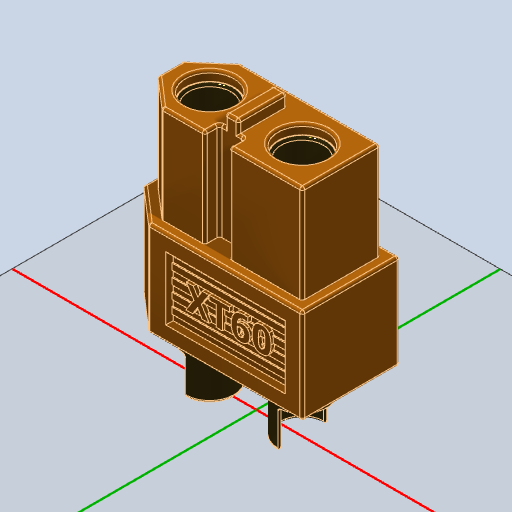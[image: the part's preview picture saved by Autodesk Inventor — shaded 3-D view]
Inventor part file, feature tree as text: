
AUTODESK INVENTOR PART (.ipt)
format: ipt  version: 2022 (Build 260153000, 153)  size: 779,776 bytes
history: native  units: mm
features: sketch x12, extrude x10, other x6, plane x4, projected_geometry x4, fillet x3, hole x1, mirror x1
ambient origin geometry x8: Origin, YZ Plane, XZ Plane, XY Plane, X Axis, Y Axis, Z Axis, Center Point
bodies: Volumenkörper1 (feature_tree)
feature tree (41):
  extrude  "Extrusion1"  Depth=8.0mm
  extrude  "Extrusion2"  Depth=3.0mm
  extrude  "Extrusion3"  Depth=3.0mm
  extrude  "Extrusion4"  Depth=0.8mm
  extrude  "Extrusion5"  Depth=1.2mm
  plane  "Arbeitsebene1"
  extrude  "Extrusion6"  TaperAngle=0.0deg  [1 undecoded]
  plane  "Arbeitsebene2"
  extrude  "Extrusion7"  Depth=4.0mm
  extrude  "Extrusion8"  Depth=8.0mm TaperAngle=0.0deg
  hole  "Bohrung1"  [1 undecoded]
  sketch  "Skizze10"  dims[d21=1.0mm d22=0.0mm d23=6.0mm]
  extrude  "Extrusion9"  Depth=6.0mm
  extrude  "Extrusion10"  Depth=4.0mm TaperAngle=0.0deg
  plane  "Arbeitsebene3"
  other  "Prägen1"
  mirror  "Spiegeln1"
  plane  "Arbeitsebene5"
  other  "Prägen2"
  fillet  "Rundung1"  [1 undecoded]
  fillet  "Rundung2"  Radius=3.5mm
  fillet  "Rundung3"  Radius=3.5mm
  sketch  "Skizze1"  dims[d0=15.6mm d1=8.0mm]
  sketch  "Skizze2"  dims[d2=2.6mm d3=3.0mm]
  sketch  "Skizze3"  dims[d4=2.6mm d5=3.0mm]
  sketch  "Skizze4"  dims[d6=7.8mm d7=0.0mm d8=0.8mm]
  sketch  "Skizze5"  dims[d9=2.0mm d10=1.2mm]
  sketch  "Skizze6"  dims[d11=6.0mm d12=0.0mm]
  sketch  "Skizze7"  dims[d13=8.0mm d14=0.0mm d15=4.0mm]
  sketch  "Skizze8"  dims[d16=4.0mm d17=8.0mm d18=0.0mm]
  projected_geometry  "Projizierte Kontur1"
  projected_geometry  "Projizierte Kontur2"
  projected_geometry  "Projizierte Kontur3"
  sketch  "Skizze9"  dims[d19=1.1mm d20=4.0mm]
  projected_geometry  "Projizierte Kontur4"
  sketch  "Skizze11"  dims[d24=6.0mm d25=4.0mm d26=0.0mm d27=-0.8mm d28=3.5mm d29=3.5mm]
  sketch  "Skizze15"  dims[d30=20.0mm d31=0.0mm d32=-3.5mm d33=2.0mm d34=0.0mm d35=2.0mm d36=3.0mm d37=2.0mm d38=3.0mm d39=1.0mm d40=0.0mm d41=3.5mm d42=6.0mm d43=4.0mm d44=2.0mm d45=90.0deg d46=0.4mm d47=20.594885mm d48=9.8mm d49=5.2mm d50=0.52mm d51=50.0mm d53=1.04mm d54=10.0mm d56=10.0mm d58=0.5mm d59=0.0mm d60=0.6mm d61=0.0mm d62=-0.4mm d63=7.0mm d66=1.4mm d67=2.0mm d68=0.3mm d69=0.0mm d78=-0.4mm d79=7.0mm d80=2.01mm d81=1.4mm d82=0.3mm d83=0.0mm d84=0.2mm d85=0.2mm d86=0.2mm]
  other  "Schnittkanten projizieren1"
  other  "Schnittkanten projizieren2"
  other  "Schnittkanten projizieren3"
  other  "Schnittkanten projizieren4"
note: 3 required parameter values undecoded (feature->parameter linkage not recoverable at this tier; creation-order binding heuristic only, values carry confidence <= 0.55)
